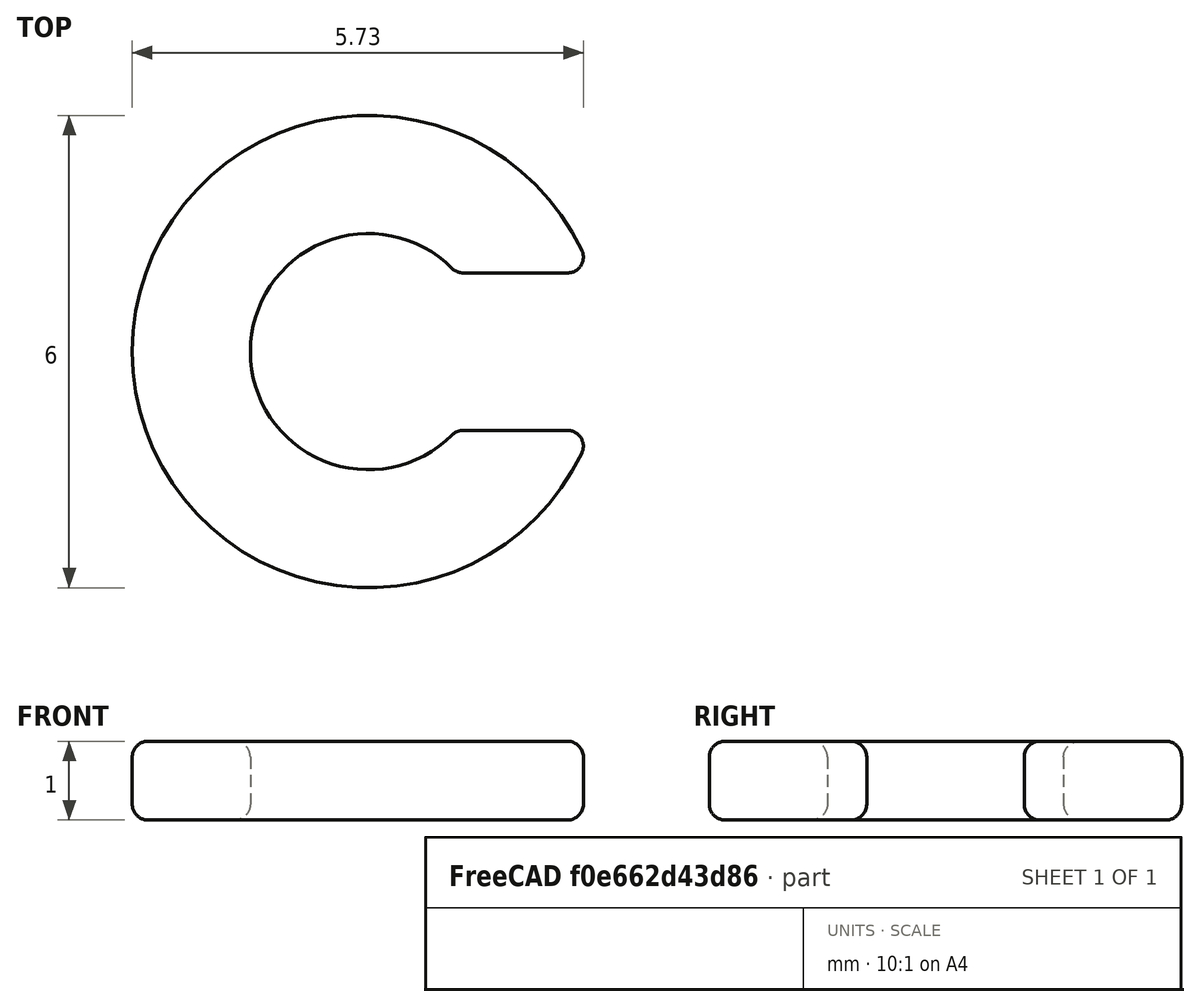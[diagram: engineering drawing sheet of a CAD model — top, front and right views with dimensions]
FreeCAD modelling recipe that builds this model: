
FCSTD DOCUMENT  (FreeCAD 1.0R1.0.1)
Label: Circlip3mm
License: All rights reserved
LicenseURL: http://en.wikipedia.org/wiki/All_rights_reserved
objects: Part::Cylinder×2, Part::Cut×2, Part::Box×1, Part::Fillet×1
note: 6 computed .brp shape members not serialized (recipe doc carries the construction recipe); baked Part::Feature solids carry a one-line shape summary decoded from their .brp

FEATURE [Part::Cylinder] Cylinder
  Angle = 360
  AttacherType = Attacher::AttachEngine3D
  FirstAngle = 0
  Height = 1
  Radius = 1.5
  SecondAngle = 0
FEATURE [Part::Cylinder] Cylinder001
  Angle = 360
  AttacherType = Attacher::AttachEngine3D
  FirstAngle = 0
  Height = 1
  Radius = 3
  SecondAngle = 0
FEATURE [Part::Cut] Cut
  Base = -> Cylinder001
  Tool = -> Cylinder
FEATURE [Part::Box] Box  label="Cube"
  AttacherType = Attacher::AttachEngine3D
  Height = 10
  Length = 3
  Placement = pos=(0,-1,0) rot=(0,0,1;0rad)
  Width = 2
FEATURE [Part::Cut] Cut001
  Base = -> Cut
  Tool = -> Box
FEATURE [Part::Fillet] Fillet  label="Seegerring3mm"
  Base = -> Cut001
  EdgeLinks = -> Cut001 [Edge1,Edge2,Edge3,Edge4,Edge5,Edge6,Edge7,Edge8,Edge9,Edge10,Edge11,Edge12]
  Edges = 12 edges r=0.2: [Edge1,Edge2,Edge3,Edge4,Edge5,Edge6,Edge7,Edge8,Edge9,Edge10,Edge11,Edge12]
